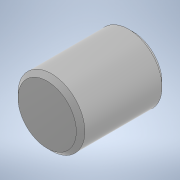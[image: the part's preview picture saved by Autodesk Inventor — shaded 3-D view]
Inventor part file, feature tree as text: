
AUTODESK INVENTOR PART (.ipt)
format: ipt  version: 2021 (Build 250183000, 183)  size: 100,352 bytes
history: native  units: mm
features: extrude x1, chamfer x1, sketch x1
ambient origin geometry x8: Origin, YZ Plane, XZ Plane, XY Plane, X Axis, Y Axis, Z Axis, Center Point
bodies: Solid1 (feature_tree)
feature tree (3):
  extrude  "Extrusion1"  Depth=10.0mm TaperAngle=0.0deg
  chamfer  "Chamfer1"  Distance=0.5mm Angle=45.0deg
  sketch  "Sketch1"  dims[d0=7.8mm d1=10.0mm d2=0.0mm d3=0.5mm d4=2.0mm d5=45.0deg]
